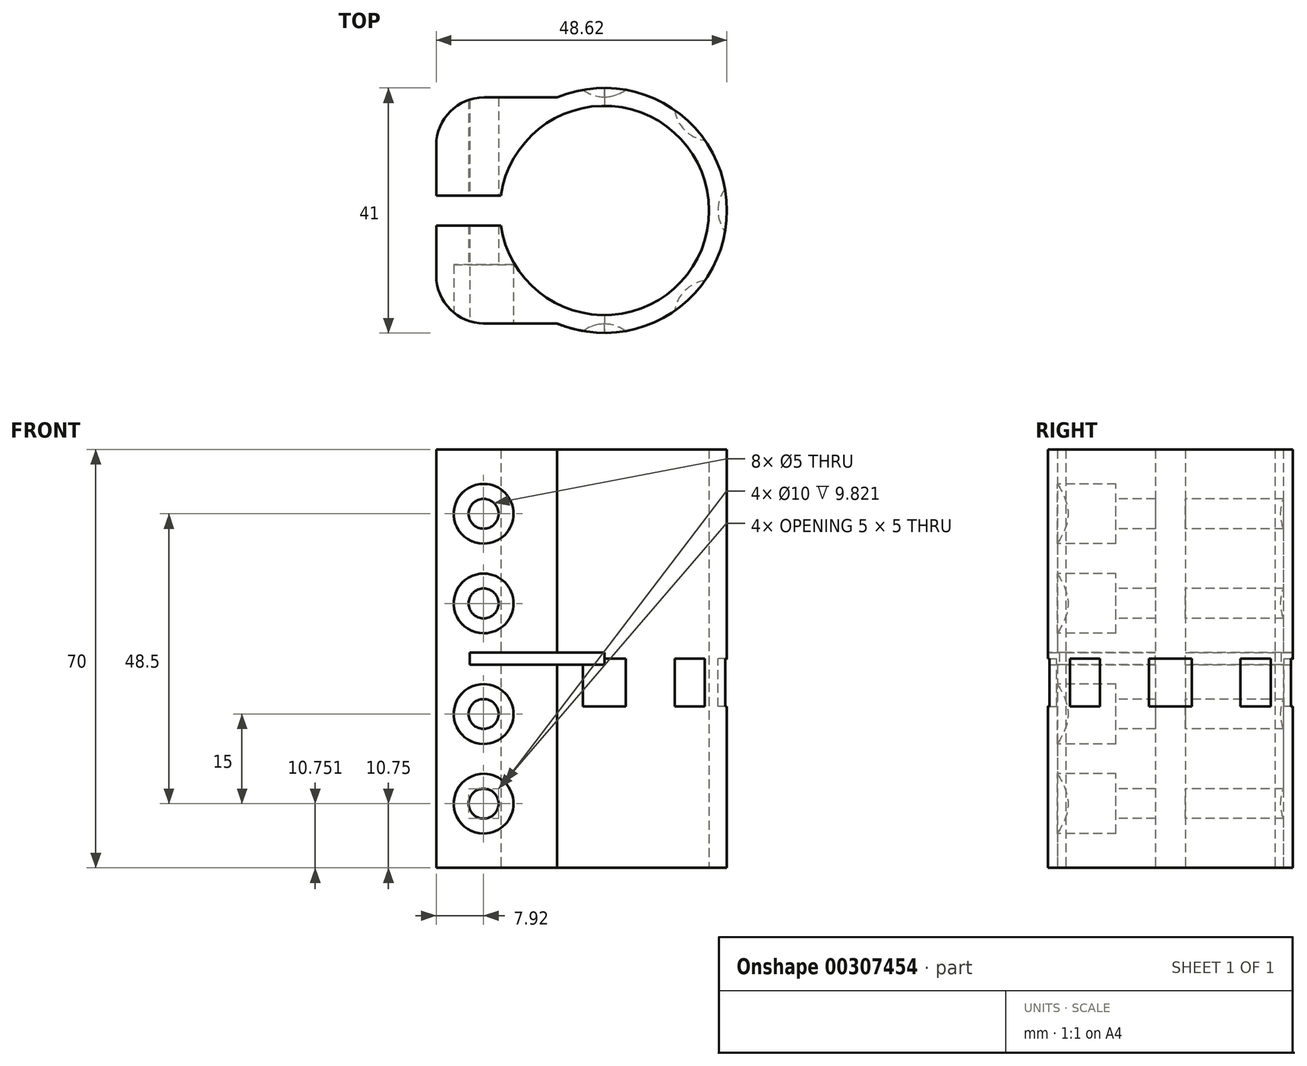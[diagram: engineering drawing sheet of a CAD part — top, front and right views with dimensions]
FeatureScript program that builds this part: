
annotation { "Feature Type Name" : "Feature", "Feature Type Description" : "" }
export const myFeature = defineFeature(function(context is Context, id is Id, definition is map)
    precondition{}
    {
        {
            var Q0;
            Q0=qCreatedBy(makeId("Top.planeOp"),FACE);
            var sketch = newSketch(context, id + "F0", { "sketchPlane" : qUnion([Q0])});
            skArc(sketch, "E0", {"start": v(-17.32, -2.5) * mm, "mid": v(17.5, 0) * mm, "end": v(-17.32, 2.5) * mm});
            skArc(sketch, "E1", {"start": v(-7.92, -18.9) * mm, "mid": v(20.5, 0) * mm, "end": v(-7.92, 18.9) * mm});
            skLineSegment(sketch, "E2", {"start": v(-28.12, 10.9) * mm, "end": v(-28.12, 2.5) * mm});
            skLineSegment(sketch, "E3", {"start": v(-28.12, 2.5) * mm, "end": v(-17.32, 2.5) * mm});
            skLineSegment(sketch, "E4", {"start": v(0, 0) * mm, "end": v(50.57, 0) * mm, "construction": true});
            skLineSegment(sketch, "E5", {"start": v(-20.12, 18.9) * mm, "end": v(-7.92, 18.9) * mm});
            skPoint(sketch, "E6.visualSharp", {"position": v(-28.12, 18.9) * mm});
            skArc(sketch, "E6.filletArc", {"start": v(-20.12, 18.9) * mm, "mid": v(-25.78, 16.57) * mm, "end": v(-28.12, 10.9) * mm});
            skLineSegment(sketch, "E7.MirrorCS", {"start": v(-28.12, -2.5) * mm, "end": v(-17.32, -2.5) * mm});
            skLineSegment(sketch, "E8.MirrorCS", {"start": v(-20.12, -18.9) * mm, "end": v(-7.92, -18.9) * mm});
            skLineSegment(sketch, "E9.MirrorCS", {"start": v(-28.12, -10.9) * mm, "end": v(-28.12, -2.5) * mm});
            skArc(sketch, "E10.MirrorCS", {"start": v(-20.12, -18.9) * mm, "mid": v(-25.78, -16.57) * mm, "end": v(-28.12, -10.9) * mm});
            skSolve(sketch);
        }
        {
            var Q0;
            Q0 = qSketchRegion(id + "F0", true);
            extrude(context, id + "F1", {"entities" : qUnion([Q0]), "endBound" : BoundingType.SYMMETRIC, "depth" : 70 * mm, "offsetDistance" : 25 * mm});
        }
        {
            var Q0;
            Q0=makeQuery(id+"F1.opExtrude","SWEPT_FACE",FACE,{"disambiguationData":[OSD([sQuery(id+"F0.wireOp",EDGE,"E8.MirrorCS")])]});
            var sketch = newSketch(context, id + "F2", { "sketchPlane" : qUnion([Q0])});
            skPoint(sketch, "E11", {"position": v(-20.2, 24.25) * mm});
            skPoint(sketch, "E12", {"position": v(-20.2, 9.25) * mm});
            skPoint(sketch, "E13", {"position": v(-20.2, -9.25) * mm});
            skPoint(sketch, "E14", {"position": v(-20.2, -24.25) * mm});
            skSolve(sketch);
        }
        {
            var Q0;
            Q0=sQuery(id+"F2.wireOp",VERTEX,"E11");
            var Q1;
            Q1=sQuery(id+"F2.wireOp",VERTEX,"E12");
            var Q2;
            Q2=sQuery(id+"F2.wireOp",VERTEX,"E13");
            var Q3;
            Q3=sQuery(id+"F2.wireOp",VERTEX,"E14");
            var Q4;
            Q4=makeQuery(id+"F1.opExtrude","SWEPT_BODY",BODY,{"disambiguationData":[OSD([sQuery(id+"F0.wireOp",EDGE,"E0"),sQuery(id+"F0.wireOp",EDGE,"E1"),sQuery(id+"F0.wireOp",EDGE,"E2"),sQuery(id+"F0.wireOp",EDGE,"E3"),sQuery(id+"F0.wireOp",EDGE,"E5"),sQuery(id+"F0.wireOp",EDGE,"E6.filletArc"),sQuery(id+"F0.wireOp",EDGE,"E7.MirrorCS"),sQuery(id+"F0.wireOp",EDGE,"E8.MirrorCS"),sQuery(id+"F0.wireOp",EDGE,"E9.MirrorCS"),sQuery(id+"F0.wireOp",EDGE,"E10.MirrorCS")])]});
            hole(context, id + "F3", {"style" : HoleStyle.C_BORE, "endStyle" : HoleEndStyle.THROUGH, "holeDiameter" : 5 * mm, "cBoreDiameter" : 10 * mm, "cBoreDepth" : 8 * mm, "isTappedThrough" : true, "tappedDepth" : 12 * mm, "tapClearance" : 3, "locations" : qUnion([Q0, Q1, Q2, Q3]), "scope" : qUnion([Q4])});
        }
        {
            var Q0;
            Q0=qCreatedBy(makeId("Front.planeOp"),FACE);
            var sketch = newSketch(context, id + "F4", { "sketchPlane" : qUnion([Q0])});
            skLineSegment(sketch, "E15.bottom", {"start": v(-22.5, 1) * mm, "end": v(0, 1) * mm});
            skLineSegment(sketch, "E15.top", {"start": v(-22.5, -1) * mm, "end": v(0, -1) * mm});
            skLineSegment(sketch, "E15.left", {"start": v(-22.5, 1) * mm, "end": v(-22.5, -1) * mm});
            skLineSegment(sketch, "E15.right", {"start": v(0, 1) * mm, "end": v(0, -1) * mm});
            skSolve(sketch);
        }
        {
            var Q0;
            Q0 = qSketchRegion(id + "F4", true);
            extrude(context, id + "F5", {"entities" : qUnion([Q0]), "operationType" : NewBodyOperationType.REMOVE, "endBound" : BoundingType.SYMMETRIC, "oppositeDirection" : true, "depth" : 50 * mm, "offsetDistance" : 25 * mm});
        }
        {
            var Q0;
            Q0=qCreatedBy(makeId("Top.planeOp"),FACE);
            var sketch = newSketch(context, id + "F6", { "sketchPlane" : qUnion([Q0])});
            skCircle(sketch, "E16", {"center": v(0, -25) * mm, "radius": 6 * mm});
            skCircle(sketch, "E17.1.0", {"center": v(17.68, -17.68) * mm, "radius": 6 * mm});
            skCircle(sketch, "E17.2.0", {"center": v(25, 0) * mm, "radius": 6 * mm});
            skCircle(sketch, "E17.3.0", {"center": v(17.68, 17.68) * mm, "radius": 6 * mm});
            skCircle(sketch, "E17.4.0", {"center": v(0, 25) * mm, "radius": 6 * mm});
            skPoint(sketch, "E17.center", {"position": v(0, 0) * mm});
            skLineSegment(sketch, "E17.anchor1", {"start": v(0, 0) * mm, "end": v(0, -25) * mm, "construction": true});
            skLineSegment(sketch, "E17.anchor2", {"start": v(0, 0) * mm, "end": v(0, 25) * mm, "construction": true});
            skSolve(sketch);
        }
        {
            var Q0;
            Q0 = qSketchRegion(id + "F6", true);
            extrude(context, id + "F7", {"entities" : qUnion([Q0]), "operationType" : NewBodyOperationType.REMOVE, "oppositeDirection" : true, "depth" : 8 * mm, "offsetDistance" : 25 * mm});
        }
    });
